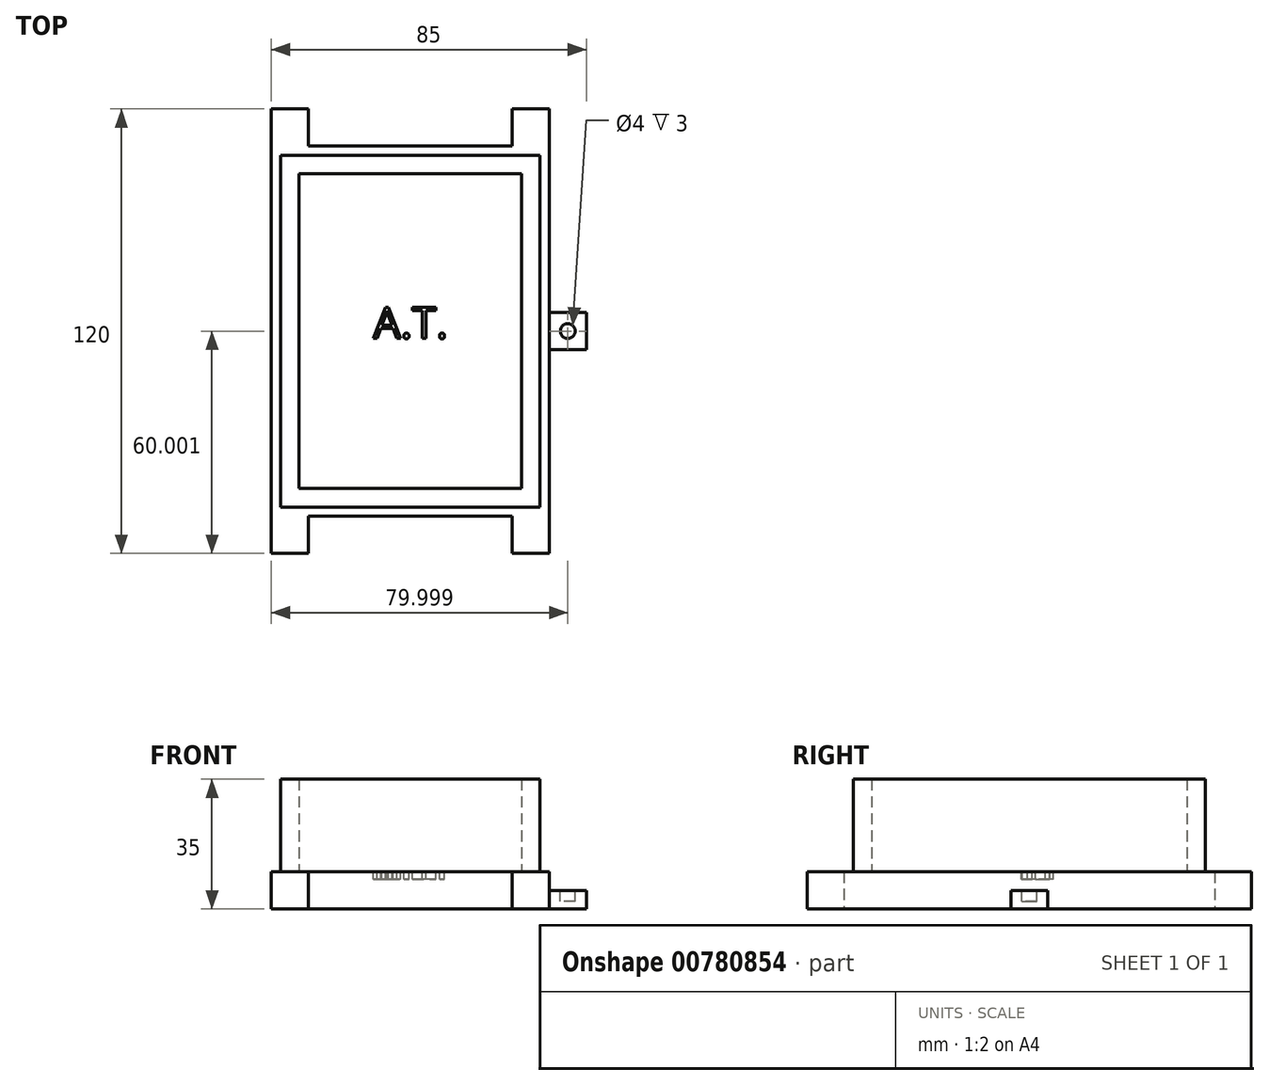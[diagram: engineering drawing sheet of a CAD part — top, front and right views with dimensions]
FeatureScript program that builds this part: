
annotation { "Feature Type Name" : "Feature", "Feature Type Description" : "" }
export const myFeature = defineFeature(function(context is Context, id is Id, definition is map)
    precondition{}
    {
        {
            var Q0;
            Q0=qCreatedBy(makeId("Top.planeOp"),FACE);
            var sketch = newSketch(context, id + "F0", { "sketchPlane" : qUnion([Q0])});
            skLineSegment(sketch, "E0.bottom", {"start": v(-95.34, -24.63) * mm, "end": v(-20.34, -24.63) * mm});
            skLineSegment(sketch, "E0.top", {"start": v(-95.34, -124.63) * mm, "end": v(-20.34, -124.63) * mm});
            skLineSegment(sketch, "E0.left", {"start": v(-95.34, -24.63) * mm, "end": v(-95.34, -124.63) * mm});
            skLineSegment(sketch, "E0.right", {"start": v(-20.34, -24.63) * mm, "end": v(-20.34, -124.63) * mm});
            skLineSegment(sketch, "E1.bottom", {"start": v(-82.84, -37.13) * mm, "end": v(-32.84, -37.13) * mm});
            skLineSegment(sketch, "E1.top", {"start": v(-82.84, -112.13) * mm, "end": v(-32.84, -112.13) * mm});
            skLineSegment(sketch, "E1.left", {"start": v(-82.84, -37.13) * mm, "end": v(-82.84, -112.13) * mm});
            skLineSegment(sketch, "E1.right", {"start": v(-32.84, -37.13) * mm, "end": v(-32.84, -112.13) * mm});
            skSolve(sketch);
        }
        {
            var Q0;
            Q0=makeQuery(id+"F0.imprint","IMPRINT",FACE,{"disambiguationData":[TD([[makeQuery(id+"F0.imprint","IMPRINT",EDGE,{"derivedFrom":sQuery(id+"F0.wireOp",EDGE,"E1.bottom")}),-1.0]])]});
            var Q1;
            Q1=makeQuery(id+"F0.imprint","IMPRINT",FACE,{"disambiguationData":[TD([[makeQuery(id+"F0.imprint","IMPRINT",EDGE,{"derivedFrom":sQuery(id+"F0.wireOp",EDGE,"E0.bottom")}),-1.0]])]});
            extrude(context, id + "F1", {"entities" : qUnion([Q0, Q1]), "depth" : 10 * mm, "offsetDistance" : 25 * mm});
        }
        {
            var Q0;
            Q0=makeQuery(id+"F1.opExtrude","CAP_FACE",FACE,{"disambiguationData":[OSD([sQuery(id+"F0.wireOp",EDGE,"E0.bottom"),sQuery(id+"F0.wireOp",EDGE,"E0.top"),sQuery(id+"F0.wireOp",EDGE,"E0.left"),sQuery(id+"F0.wireOp",EDGE,"E0.right")])],"isStart":false});
            var sketch = newSketch(context, id + "F2", { "sketchPlane" : qUnion([Q0])});
            skLineSegment(sketch, "E2.bottom", {"start": v(-87.84, -32.13) * mm, "end": v(-27.84, -32.13) * mm});
            skLineSegment(sketch, "E2.top", {"start": v(-87.84, -117.13) * mm, "end": v(-27.84, -117.13) * mm});
            skLineSegment(sketch, "E2.left", {"start": v(-87.84, -32.13) * mm, "end": v(-87.84, -117.13) * mm});
            skLineSegment(sketch, "E2.right", {"start": v(-27.84, -32.13) * mm, "end": v(-27.84, -117.13) * mm});
            skLineSegment(sketch, "E3.bottom", {"start": v(-92.84, -27.13) * mm, "end": v(-22.84, -27.13) * mm});
            skLineSegment(sketch, "E3.top", {"start": v(-92.84, -122.13) * mm, "end": v(-22.84, -122.13) * mm});
            skLineSegment(sketch, "E3.left", {"start": v(-92.84, -27.13) * mm, "end": v(-92.84, -122.13) * mm});
            skLineSegment(sketch, "E3.right", {"start": v(-22.84, -27.13) * mm, "end": v(-22.84, -122.13) * mm});
            skSolve(sketch);
        }
        {
            var Q0;
            Q0=makeQuery(id+"F2.imprint","IMPRINT",FACE,{"disambiguationData":[TD([[makeQuery(id+"F2.imprint","IMPRINT",EDGE,{"derivedFrom":sQuery(id+"F2.wireOp",EDGE,"E2.bottom")}),1.0]])]});
            extrude(context, id + "F3", {"entities" : qUnion([Q0]), "operationType" : NewBodyOperationType.ADD, "depth" : 25 * mm, "offsetDistance" : 25 * mm});
        }
        {
            var Q0;
            Q0=makeQuery(id+"F1.opExtrude","SWEPT_FACE",FACE,{"disambiguationData":[OSD([sQuery(id+"F0.wireOp",EDGE,"E0.top")])]});
            var sketch = newSketch(context, id + "F4", { "sketchPlane" : qUnion([Q0])});
            skLineSegment(sketch, "E4.bottom", {"start": v(-95.34, 10) * mm, "end": v(-85.34, 10) * mm});
            skLineSegment(sketch, "E4.top", {"start": v(-95.34, 0) * mm, "end": v(-85.34, 0) * mm});
            skLineSegment(sketch, "E4.left", {"start": v(-95.34, 10) * mm, "end": v(-95.34, 0) * mm});
            skLineSegment(sketch, "E4.right", {"start": v(-85.34, 10) * mm, "end": v(-85.34, 0) * mm});
            skLineSegment(sketch, "E5.bottom", {"start": v(-20.34, 10) * mm, "end": v(-30.34, 10) * mm});
            skLineSegment(sketch, "E5.top", {"start": v(-20.34, 0) * mm, "end": v(-30.34, 0) * mm});
            skLineSegment(sketch, "E5.left", {"start": v(-20.34, 10) * mm, "end": v(-20.34, 0) * mm});
            skLineSegment(sketch, "E5.right", {"start": v(-30.34, 10) * mm, "end": v(-30.34, 0) * mm});
            skSolve(sketch);
        }
        {
            var Q0;
            Q0=makeQuery(id+"F4.imprint","IMPRINT",FACE,{"disambiguationData":[TD([[makeQuery(id+"F4.imprint","IMPRINT",EDGE,{"derivedFrom":sQuery(id+"F4.wireOp",EDGE,"E5.bottom")}),-1.0]])]});
            var Q1;
            Q1=makeQuery(id+"F4.imprint","IMPRINT",FACE,{"disambiguationData":[TD([[makeQuery(id+"F4.imprint","IMPRINT",EDGE,{"derivedFrom":sQuery(id+"F4.wireOp",EDGE,"E4.bottom")}),-1.0]])]});
            extrude(context, id + "F5", {"entities" : qUnion([Q0, Q1]), "operationType" : NewBodyOperationType.ADD, "depth" : 10 * mm, "offsetDistance" : 25 * mm});
        }
        {
            var Q0;
            Q0=makeQuery(id+"F1.opExtrude","SWEPT_FACE",FACE,{"disambiguationData":[OSD([sQuery(id+"F0.wireOp",EDGE,"E0.bottom")])]});
            var sketch = newSketch(context, id + "F6", { "sketchPlane" : qUnion([Q0])});
            skLineSegment(sketch, "E6.bottom", {"start": v(20.34, 10) * mm, "end": v(30.34, 10) * mm});
            skLineSegment(sketch, "E6.top", {"start": v(20.34, 0) * mm, "end": v(30.34, 0) * mm});
            skLineSegment(sketch, "E6.left", {"start": v(20.34, 10) * mm, "end": v(20.34, 0) * mm});
            skLineSegment(sketch, "E6.right", {"start": v(30.34, 10) * mm, "end": v(30.34, 0) * mm});
            skLineSegment(sketch, "E7.bottom", {"start": v(95.34, 10) * mm, "end": v(85.34, 10) * mm});
            skLineSegment(sketch, "E7.top", {"start": v(95.34, 0) * mm, "end": v(85.34, 0) * mm});
            skLineSegment(sketch, "E7.left", {"start": v(95.34, 10) * mm, "end": v(95.34, 0) * mm});
            skLineSegment(sketch, "E7.right", {"start": v(85.34, 10) * mm, "end": v(85.34, 0) * mm});
            skSolve(sketch);
        }
        {
            var Q0;
            Q0 = qSketchRegion(id + "F6", true);
            extrude(context, id + "F7", {"entities" : qUnion([Q0]), "operationType" : NewBodyOperationType.ADD, "depth" : 10 * mm, "offsetDistance" : 25 * mm});
        }
        {
            var Q0;
            Q0=makeQuery(id+"F7.boolean.opBoolean","MERGE",FACE,{"derivedFrom":[makeQuery(id+"F5.boolean.opBoolean","MERGE",FACE,{"derivedFrom":[makeQuery(id+"F1.opExtrude","SWEPT_FACE",FACE,{"disambiguationData":[OSD([sQuery(id+"F0.wireOp",EDGE,"E0.right")])]}),makeQuery(id+"F5.opExtrude","SWEPT_FACE",FACE,{"disambiguationData":[OSD([sQuery(id+"F4.wireOp",EDGE,"E5.left")])]})]}),makeQuery(id+"F7.opExtrude","SWEPT_FACE",FACE,{"disambiguationData":[OSD([sQuery(id+"F6.wireOp",EDGE,"E6.left")])]})]});
            var sketch = newSketch(context, id + "F8", { "sketchPlane" : qUnion([Q0])});
            skLineSegment(sketch, "E8.bottom", {"start": v(-79.63, 0) * mm, "end": v(-69.63, 0) * mm});
            skLineSegment(sketch, "E8.top", {"start": v(-79.63, 5) * mm, "end": v(-69.63, 5) * mm});
            skLineSegment(sketch, "E8.left", {"start": v(-79.63, 0) * mm, "end": v(-79.63, 5) * mm});
            skLineSegment(sketch, "E8.right", {"start": v(-69.63, 0) * mm, "end": v(-69.63, 5) * mm});
            skSolve(sketch);
        }
        {
            var Q0;
            Q0=makeQuery(id+"F8.imprint","IMPRINT",FACE,{"disambiguationData":[TD([[makeQuery(id+"F8.imprint","IMPRINT",EDGE,{"derivedFrom":sQuery(id+"F8.wireOp",EDGE,"E8.bottom")}),-1.0]])]});
            extrude(context, id + "F9", {"entities" : qUnion([Q0]), "operationType" : NewBodyOperationType.ADD, "depth" : 10 * mm, "offsetDistance" : 25 * mm});
        }
        {
            var Q0;
            Q0=makeQuery(id+"F9.opExtrude","SWEPT_FACE",FACE,{"disambiguationData":[OSD([sQuery(id+"F8.wireOp",EDGE,"E8.top")])]});
            var sketch = newSketch(context, id + "F10", { "sketchPlane" : qUnion([Q0])});
            skCircle(sketch, "E9", {"center": v(-15.34, -74.63) * mm, "radius": 2 * mm});
            skSolve(sketch);
        }
        {
            var Q0;
            Q0=makeQuery(id+"FojpXLmNnNwP5Uy_1.imprint","IMPRINT",FACE,{"disambiguationData":[TD([[makeQuery(id+"FojpXLmNnNwP5Uy_1.imprint","IMPRINT",EDGE,{"derivedFrom":sQuery(id+"FojpXLmNnNwP5Uy_1.wireOp",EDGE,"44UxGHVO-p44D-4ubh-eXjl-kveCB1PUPdid")}),1.0]])]});
            var Q1;
            Q1=makeQuery(id+"F10.imprint","IMPRINT",FACE,{"disambiguationData":[TD([[makeQuery(id+"F10.imprint","IMPRINT",EDGE,{"derivedFrom":sQuery(id+"F10.wireOp",EDGE,"E9")}),1.0]])]});
            var Q2;
            Q2=makeQuery(id+"FojpXLmNnNwP5Uy_1.imprint","IMPRINT",FACE,{"disambiguationData":[TD([[makeQuery(id+"FojpXLmNnNwP5Uy_1.imprint","IMPRINT",EDGE,{"derivedFrom":sQuery(id+"FojpXLmNnNwP5Uy_1.wireOp",EDGE,"lmHB0SYF-jleA-0Wqv-PTPo-NTpha4ZxZ82f")}),1.0]])]});
            extrude(context, id + "F11", {"entities" : qUnion([Q0, Q1, Q2]), "operationType" : NewBodyOperationType.REMOVE, "oppositeDirection" : true, "depth" : 3 * mm, "offsetDistance" : 25 * mm});
        }
        {
            var Q0;
            Q0=makeQuery(id+"F3.boolean.opBoolean","SPLIT",FACE,{"disambiguationData":[TD([makeQuery(id+"F3.opExtrude","SWEPT_FACE",FACE,{"disambiguationData":[OSD([sQuery(id+"F2.wireOp",EDGE,"E2.bottom")])]})])],"derivedFrom":makeQuery(id+"F1.opExtrude","CAP_FACE",FACE,{"disambiguationData":[OSD([sQuery(id+"F0.wireOp",EDGE,"E0.bottom"),sQuery(id+"F0.wireOp",EDGE,"E0.top"),sQuery(id+"F0.wireOp",EDGE,"E0.left"),sQuery(id+"F0.wireOp",EDGE,"E0.right")])],"isStart":false})});
            var sketch = newSketch(context, id + "F12", { "sketchPlane" : qUnion([Q0])});
            skText(sketch, "E10", { "text": "A.T.", "fontName": "OpenSans-Regular.ttf"});
            const initialGuessF12  = {"E10": [-0.06784, -0.07656, 1, 0, 0.00843]};
            skSetInitialGuess(sketch, initialGuessF12);
            skSolve(sketch);
        }
        {
            var Q0;
            Q0 = qSketchRegion(id + "F12", true);
            extrude(context, id + "F13", {"entities" : qUnion([Q0]), "operationType" : NewBodyOperationType.REMOVE, "oppositeDirection" : true, "depth" : 2 * mm, "offsetDistance" : 25 * mm});
        }
    });
